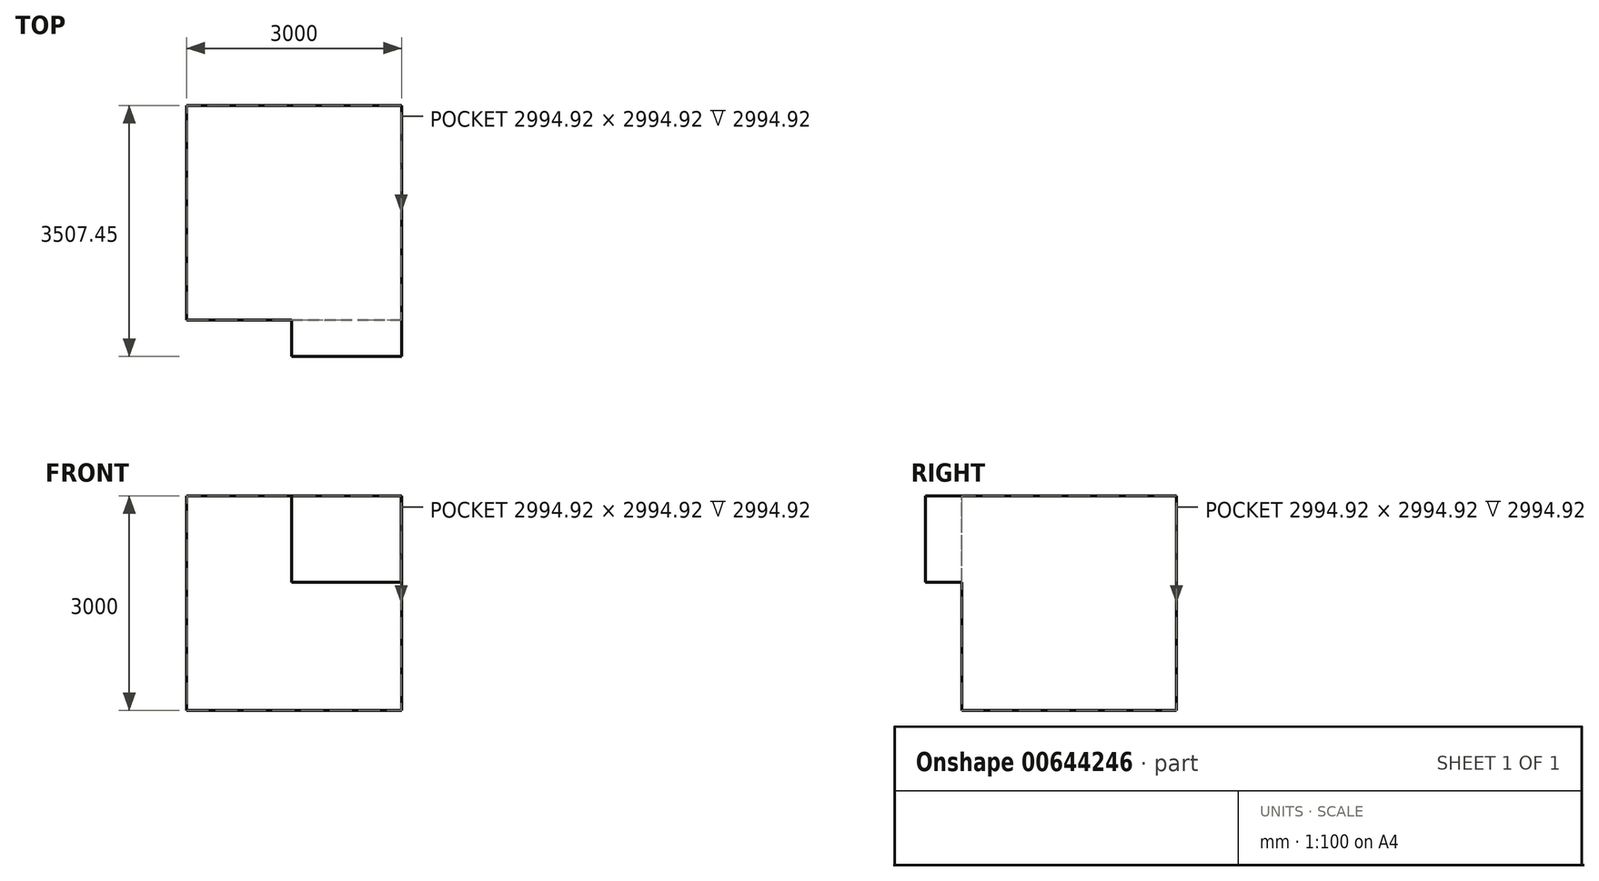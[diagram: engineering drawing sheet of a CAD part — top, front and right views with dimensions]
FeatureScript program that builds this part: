
annotation { "Feature Type Name" : "Feature", "Feature Type Description" : "" }
export const myFeature = defineFeature(function(context is Context, id is Id, definition is map)
    precondition{}
    {
        {
            var Q0;
            Q0=qCreatedBy(makeId("Top.planeOp"),FACE);
            var sketch = newSketch(context, id + "F0", { "sketchPlane" : qUnion([Q0])});
            skLineSegment(sketch, "E0", {"start": v(0, 0) * mm, "end": v(0, 3000) * mm});
            skLineSegment(sketch, "E1", {"start": v(0, 3000) * mm, "end": v(3000, 3000) * mm});
            skLineSegment(sketch, "E2", {"start": v(3000, 3000) * mm, "end": v(3000, 0) * mm});
            skLineSegment(sketch, "E3", {"start": v(3000, 0) * mm, "end": v(0, 0) * mm});
            skSolve(sketch);
        }
        {
            var Q0;
            Q0=makeQuery(id+"F0.imprint","IMPRINT",FACE,{"disambiguationData":[TD([[makeQuery(id+"F0.imprint","IMPRINT",EDGE,{"derivedFrom":sQuery(id+"F0.wireOp",EDGE,"E0")}),-1.0]])]});
            var sketch = newSketch(context, id + "F1", { "sketchPlane" : qUnion([Q0])});
            skLineSegment(sketch, "E4.0", {"start": v(3000, 0) * mm, "end": v(0, 0) * mm});
            skSolve(sketch);
        }
        {
            var Q0;
            Q0 = qSketchRegion(id + "F1", true);
            var Q1;
            Q1=makeQuery(id+"F0.imprint","IMPRINT",FACE,{"disambiguationData":[TD([[makeQuery(id+"F0.imprint","IMPRINT",EDGE,{"derivedFrom":sQuery(id+"F0.wireOp",EDGE,"E0")}),-1.0]])]});
            extrude(context, id + "F2", {"entities" : qUnion([Q0, Q1]), "oppositeDirection" : true, "depth" : 3000 * mm, "offsetDistance" : 25.4 * mm});
        }
        {
            var Q0;
            Q0=makeQuery(id+"F2.opExtrude","SWEPT_FACE",FACE,{"disambiguationData":[OSD([sQuery(id+"F0.wireOp",EDGE,"E3")])]});
            var sketch = newSketch(context, id + "F3", { "sketchPlane" : qUnion([Q0])});
            skLineSegment(sketch, "E5.bottom", {"start": v(1466.09, -1206.46) * mm, "end": v(3000, -1206.46) * mm});
            skLineSegment(sketch, "E5.top", {"start": v(1466.09, 0) * mm, "end": v(3000, 0) * mm});
            skLineSegment(sketch, "E5.left", {"start": v(1466.09, -1206.46) * mm, "end": v(1466.09, 0) * mm});
            skLineSegment(sketch, "E5.right", {"start": v(3000, -1206.46) * mm, "end": v(3000, 0) * mm});
            skSolve(sketch);
        }
        {
            var Q0;
            Q0=makeQuery(id+"F3.imprint","IMPRINT",FACE,{"disambiguationData":[TD([[makeQuery(id+"F3.imprint","IMPRINT",EDGE,{"derivedFrom":sQuery(id+"F3.wireOp",EDGE,"E5.bottom")}),1.0]])]});
            extrude(context, id + "F4", {"entities" : qUnion([Q0]), "operationType" : NewBodyOperationType.ADD, "depth" : 456.65 * mm, "offsetDistance" : 25.4 * mm});
        }
        {
            var Q0;
            Q0=makeQuery(id+"F2.opExtrude","SWEPT_FACE",FACE,{"disambiguationData":[OSD([sQuery(id+"F0.wireOp",EDGE,"E3")])]});
            var sketch = newSketch(context, id + "F5", { "sketchPlane" : qUnion([Q0])});
            skLineSegment(sketch, "E6.bottom", {"start": v(1226.08, -1191.15) * mm, "end": v(422.56, -1191.15) * mm});
            skLineSegment(sketch, "E6.top", {"start": v(1226.08, -151.8) * mm, "end": v(422.56, -151.8) * mm});
            skLineSegment(sketch, "E6.left", {"start": v(1226.08, -1191.15) * mm, "end": v(1226.08, -151.8) * mm});
            skLineSegment(sketch, "E6.right", {"start": v(422.56, -1191.15) * mm, "end": v(422.56, -151.8) * mm});
            skSolve(sketch);
        }
        {
            var Q0;
            Q0=makeQuery(id+"F4.opExtrude","CAP_FACE",FACE,{"disambiguationData":[OSD([sQuery(id+"F3.wireOp",EDGE,"E5.bottom"),sQuery(id+"F3.wireOp",EDGE,"E5.top"),sQuery(id+"F3.wireOp",EDGE,"E5.left"),sQuery(id+"F3.wireOp",EDGE,"E5.right")])],"isStart":false});
            extrude(context, id + "F6", {"entities" : qUnion([Q0]), "operationType" : NewBodyOperationType.ADD, "oppositeDirection" : true, "depth" : 7.78 * mm, "offsetDistance" : 25.4 * mm});
        }
        {
            var Q0;
            Q0=makeQuery(id+"F4.opExtrude","CAP_FACE",FACE,{"disambiguationData":[OSD([sQuery(id+"F3.wireOp",EDGE,"E5.bottom"),sQuery(id+"F3.wireOp",EDGE,"E5.top"),sQuery(id+"F3.wireOp",EDGE,"E5.left"),sQuery(id+"F3.wireOp",EDGE,"E5.right")])],"isStart":false});
            extrude(context, id + "F7", {"entities" : qUnion([Q0]), "operationType" : NewBodyOperationType.ADD, "depth" : 25.4 * mm, "offsetDistance" : 25.4 * mm});
        }
        {
            var Q0;
            Q0=makeQuery(id+"F7.opExtrude","CAP_FACE",FACE,{"disambiguationData":[OSD([sQuery(id+"F3.wireOp",EDGE,"E5.bottom"),sQuery(id+"F3.wireOp",EDGE,"E5.top"),sQuery(id+"F3.wireOp",EDGE,"E5.left"),sQuery(id+"F3.wireOp",EDGE,"E5.right")])],"isStart":false});
            extrude(context, id + "F8", {"entities" : qUnion([Q0]), "operationType" : NewBodyOperationType.ADD, "depth" : 25.4 * mm, "offsetDistance" : 25.4 * mm});
        }
        {
            var Q0;
            Q0=makeQuery(id+"F8.opExtrude","CAP_FACE",FACE,{"disambiguationData":[OSD([sQuery(id+"F3.wireOp",EDGE,"E5.bottom"),sQuery(id+"F3.wireOp",EDGE,"E5.top"),sQuery(id+"F3.wireOp",EDGE,"E5.left"),sQuery(id+"F3.wireOp",EDGE,"E5.right")])],"isStart":false});
            shell(context, id + "F9", {"entities" : qUnion([Q0]), "thickness" : 2.54 * mm});
        }
    });
